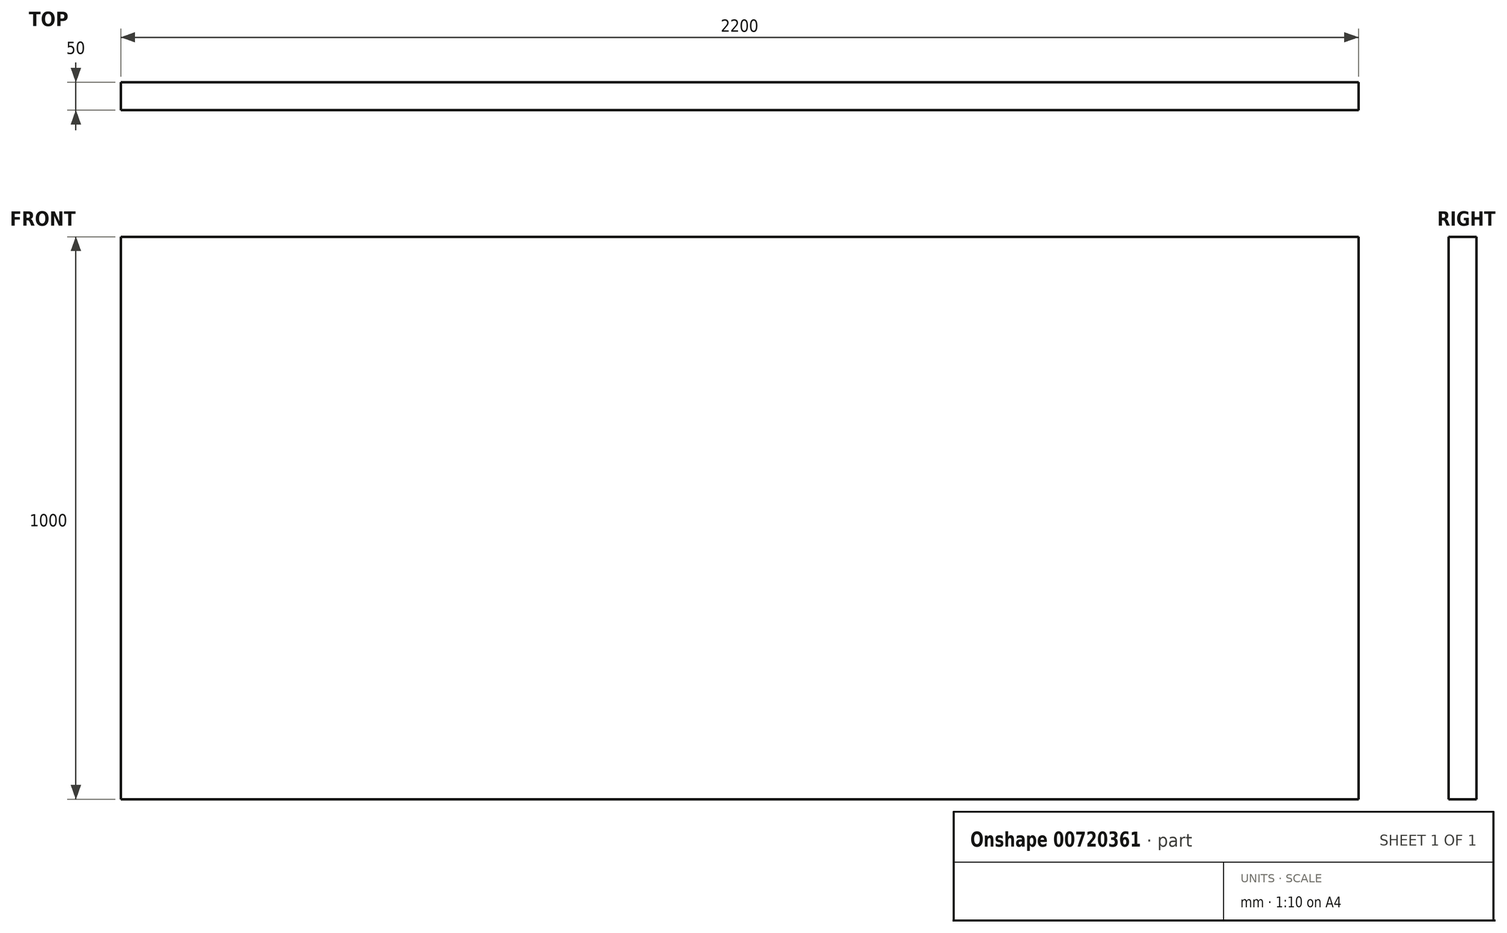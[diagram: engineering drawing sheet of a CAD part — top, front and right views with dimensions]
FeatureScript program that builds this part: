
annotation { "Feature Type Name" : "Feature", "Feature Type Description" : "" }
export const myFeature = defineFeature(function(context is Context, id is Id, definition is map)
    precondition{}
    {
        {
            var Q0;
            Q0=qCreatedBy(makeId("Front.planeOp"),FACE);
            var sketch = newSketch(context, id + "F0", { "sketchPlane" : qUnion([Q0])});
            skLineSegment(sketch, "E0.bottom", {"start": v(1100, -500) * mm, "end": v(-1100, -500) * mm});
            skLineSegment(sketch, "E0.top", {"start": v(1100, 500) * mm, "end": v(-1100, 500) * mm});
            skLineSegment(sketch, "E0.left", {"start": v(1100, -500) * mm, "end": v(1100, 500) * mm});
            skLineSegment(sketch, "E0.right", {"start": v(-1100, -500) * mm, "end": v(-1100, 500) * mm});
            skPoint(sketch, "E0.middle", {"position": v(0, 0) * mm});
            skSolve(sketch);
        }
        {
            var Q0;
            Q0=makeQuery(id+"F0.imprint","IMPRINT",FACE,{"disambiguationData":[TD([[makeQuery(id+"F0.imprint","IMPRINT",EDGE,{"derivedFrom":sQuery(id+"F0.wireOp",EDGE,"E0.bottom")}),-1.0]])]});
            extrude(context, id + "F1", {"entities" : qUnion([Q0]), "depth" : 50 * mm, "offsetDistance" : 25 * mm});
        }
    });
